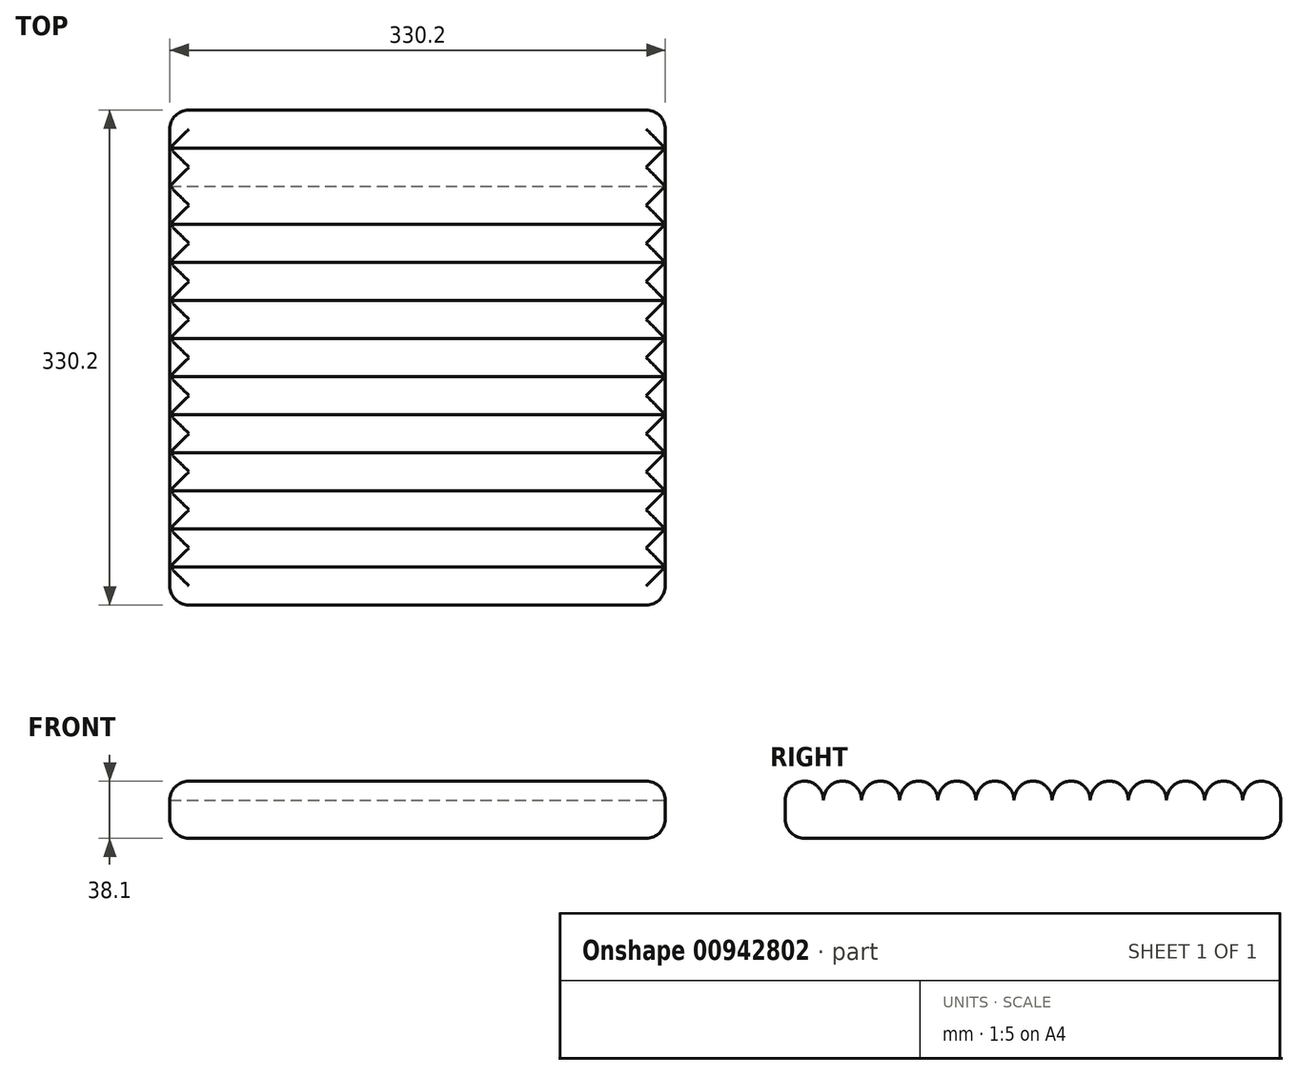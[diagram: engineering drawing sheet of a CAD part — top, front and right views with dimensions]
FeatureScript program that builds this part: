
annotation { "Feature Type Name" : "Feature", "Feature Type Description" : "" }
export const myFeature = defineFeature(function(context is Context, id is Id, definition is map)
    precondition{}
    {
        {
            var Q0;
            Q0=qCreatedBy(makeId("Top.planeOp"),FACE);
            var sketch = newSketch(context, id + "F0", { "sketchPlane" : qUnion([Q0])});
            skLineSegment(sketch, "E0.bottom", {"start": v(0, 0) * mm, "end": v(330.2, 0) * mm});
            skLineSegment(sketch, "E0.top", {"start": v(0, 330.2) * mm, "end": v(330.2, 330.2) * mm});
            skLineSegment(sketch, "E0.left", {"start": v(0, 0) * mm, "end": v(0, 330.2) * mm});
            skLineSegment(sketch, "E0.right", {"start": v(330.2, 0) * mm, "end": v(330.2, 330.2) * mm});
            skSolve(sketch);
        }
        {
            var Q0;
            Q0=qSketchRegion(id+"F0",true);
            extrude(context, id + "F1", {"entities" : qUnion([Q0]), "depth" : 38.1 * mm, "offsetDistance" : 25.4 * mm});
        }
        {
            var Q0;
            Q0=makeQuery(id+"F1.opExtrude","CAP_FACE",FACE,{"disambiguationData":[OSD([sQuery(id+"F0.wireOp",EDGE,"E0.bottom"),sQuery(id+"F0.wireOp",EDGE,"E0.top"),sQuery(id+"F0.wireOp",EDGE,"E0.left"),sQuery(id+"F0.wireOp",EDGE,"E0.right")])],"isStart":false});
            var Q1;
            Q1=makeQuery(id+"F1.opExtrude","CAP_FACE",FACE,{"disambiguationData":[OSD([sQuery(id+"F0.wireOp",EDGE,"E0.bottom"),sQuery(id+"F0.wireOp",EDGE,"E0.top"),sQuery(id+"F0.wireOp",EDGE,"E0.left"),sQuery(id+"F0.wireOp",EDGE,"E0.right")])],"isStart":true});
            fillet(context, id + "F2", {"entities" : qUnion([Q0, Q1]), "radius" : 12.7 * mm, "tangentPropagation" : true, "allowEdgeOverflow" : false});
        }
        {
            var Q0;
            Q0=makeQuery(id+"F1.opExtrude","SWEPT_EDGE",EDGE,{"disambiguationData":[OSD([sQuery(id+"F0.wireOp",EDGE,"E0.bottom"),sQuery(id+"F0.wireOp",EDGE,"E0.left")])]});
            var Q1;
            Q1=makeQuery(id+"F1.opExtrude","SWEPT_EDGE",EDGE,{"disambiguationData":[OSD([sQuery(id+"F0.wireOp",EDGE,"E0.top"),sQuery(id+"F0.wireOp",EDGE,"E0.left")])]});
            var Q2;
            Q2=makeQuery(id+"F1.opExtrude","SWEPT_EDGE",EDGE,{"disambiguationData":[OSD([sQuery(id+"F0.wireOp",EDGE,"E0.top"),sQuery(id+"F0.wireOp",EDGE,"E0.right")])]});
            var Q3;
            Q3=makeQuery(id+"F1.opExtrude","SWEPT_EDGE",EDGE,{"disambiguationData":[OSD([sQuery(id+"F0.wireOp",EDGE,"E0.bottom"),sQuery(id+"F0.wireOp",EDGE,"E0.right")])]});
            fillet(context, id + "F3", {"entities" : qUnion([Q0, Q1, Q2, Q3]), "radius" : 12.7 * mm, "tangentPropagation" : true, "allowEdgeOverflow" : false});
        }
        {
            var Q0;
            Q0=makeQuery(id+"F1.opExtrude","SWEPT_FACE",FACE,{"disambiguationData":[OSD([sQuery(id+"F0.wireOp",EDGE,"E0.right")])]});
            var sketch = newSketch(context, id + "F4", { "sketchPlane" : qUnion([Q0])});
            skLineSegment(sketch, "E1.0", {"start": v(12.7, 38.1) * mm, "end": v(317.5, 38.1) * mm, "construction": true});
            skLineSegment(sketch, "E2.0", {"start": v(317.5, 25.4) * mm, "end": v(317.5, 38.1) * mm, "construction": true});
            skLineSegment(sketch, "E3.0", {"start": v(317.5, 25.4) * mm, "end": v(12.7, 25.4) * mm, "construction": true});
            skLineSegment(sketch, "E4.0", {"start": v(12.7, 38.1) * mm, "end": v(12.7, 25.4) * mm, "construction": true});
            skArc(sketch, "E5", {"start": v(12.7, 38.1) * mm, "mid": v(21.68, 34.38) * mm, "end": v(25.4, 25.4) * mm});
            skArc(sketch, "E6", {"start": v(50.8, 25.4) * mm, "mid": v(38.1, 38.1) * mm, "end": v(25.4, 25.4) * mm});
            skArc(sketch, "E7", {"start": v(76.2, 25.4) * mm, "mid": v(63.5, 38.1) * mm, "end": v(50.8, 25.4) * mm});
            skArc(sketch, "E8", {"start": v(101.6, 25.4) * mm, "mid": v(88.9, 38.1) * mm, "end": v(76.2, 25.4) * mm});
            skArc(sketch, "E9", {"start": v(127, 25.4) * mm, "mid": v(114.3, 38.1) * mm, "end": v(101.6, 25.4) * mm});
            skArc(sketch, "E10", {"start": v(152.4, 25.4) * mm, "mid": v(139.7, 38.1) * mm, "end": v(127, 25.4) * mm});
            skArc(sketch, "E11", {"start": v(177.8, 25.4) * mm, "mid": v(165.1, 38.1) * mm, "end": v(152.4, 25.4) * mm});
            skArc(sketch, "E12", {"start": v(203.2, 25.4) * mm, "mid": v(190.5, 38.1) * mm, "end": v(177.8, 25.4) * mm});
            skArc(sketch, "E13", {"start": v(228.6, 25.4) * mm, "mid": v(215.9, 38.1) * mm, "end": v(203.2, 25.4) * mm});
            skArc(sketch, "E14", {"start": v(254, 25.4) * mm, "mid": v(241.3, 38.1) * mm, "end": v(228.6, 25.4) * mm});
            skArc(sketch, "E15", {"start": v(279.4, 25.4) * mm, "mid": v(266.7, 38.1) * mm, "end": v(254, 25.4) * mm});
            skArc(sketch, "E16", {"start": v(304.8, 25.4) * mm, "mid": v(292.1, 38.1) * mm, "end": v(279.4, 25.4) * mm});
            skArc(sketch, "E17", {"start": v(330.2, 25.4) * mm, "mid": v(317.5, 38.1) * mm, "end": v(304.8, 25.4) * mm});
            skArc(sketch, "E18", {"start": v(304.8, 25.4) * mm, "mid": v(308.52, 34.38) * mm, "end": v(317.5, 38.1) * mm});
            skLineSegment(sketch, "E19", {"start": v(12.7, 38.1) * mm, "end": v(317.5, 38.1) * mm});
            skSolve(sketch);
        }
        {
            var Q0;
            Q0=qSketchRegion(id+"F4",true);
            extrude(context, id + "F5", {"entities" : qUnion([Q0]), "operationType" : NewBodyOperationType.REMOVE, "endBound" : BoundingType.THROUGH_ALL, "oppositeDirection" : true, "depth" : 25.4 * mm, "offsetDistance" : 25.4 * mm});
        }
    });
